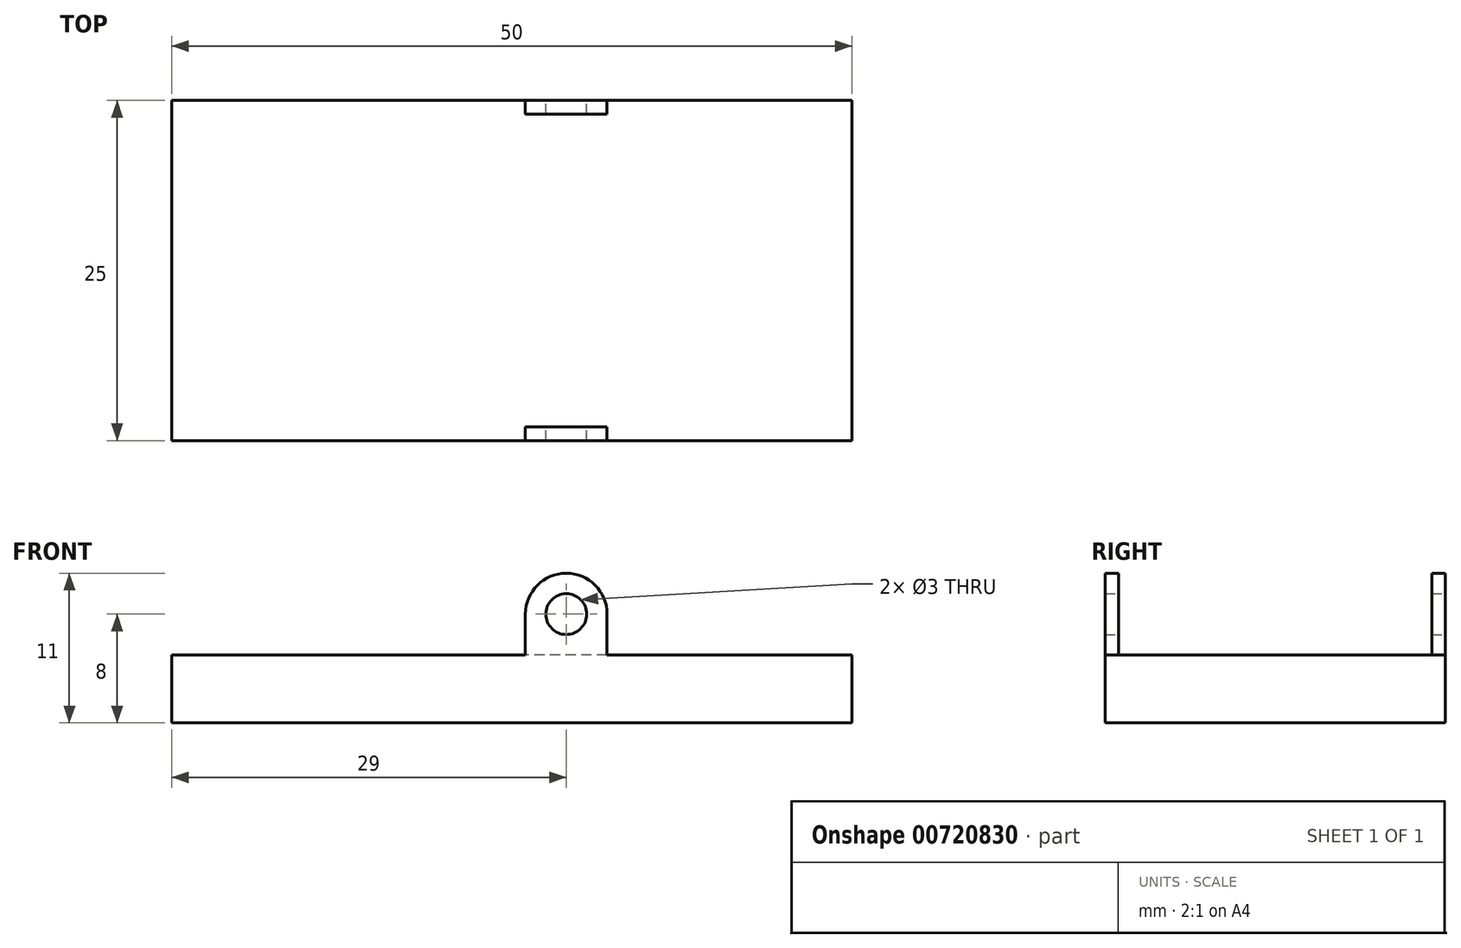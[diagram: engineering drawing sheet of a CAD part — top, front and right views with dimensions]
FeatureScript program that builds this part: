
annotation { "Feature Type Name" : "Feature", "Feature Type Description" : "" }
export const myFeature = defineFeature(function(context is Context, id is Id, definition is map)
    precondition{}
    {
        {
            var Q0;
            Q0=qCreatedBy(makeId("Top.planeOp"),FACE);
            var sketch = newSketch(context, id + "F0", { "sketchPlane" : qUnion([Q0])});
            skLineSegment(sketch, "E0.bottom", {"start": v(20, -12.5) * mm, "end": v(-20, -12.5) * mm});
            skLineSegment(sketch, "E0.top", {"start": v(20, 12.5) * mm, "end": v(-20, 12.5) * mm});
            skLineSegment(sketch, "E0.left", {"start": v(20, -12.5) * mm, "end": v(20, 12.5) * mm});
            skLineSegment(sketch, "E0.right", {"start": v(-20, -12.5) * mm, "end": v(-20, 12.5) * mm});
            skPoint(sketch, "E0.middle", {"position": v(0, 0) * mm});
            skSolve(sketch);
        }
        {
            var Q0;
            Q0=makeQuery(id+"F0.imprint","IMPRINT",FACE,{"disambiguationData":[TD([[makeQuery(id+"F0.imprint","IMPRINT",EDGE,{"derivedFrom":sQuery(id+"F0.wireOp",EDGE,"E0.bottom")}),-1.0]])]});
            extrude(context, id + "F1", {"entities" : qUnion([Q0]), "depth" : 5 * mm, "offsetDistance" : 25 * mm});
        }
        {
            var Q0;
            Q0=makeQuery(id+"F1.opExtrude","CAP_FACE",FACE,{"disambiguationData":[OSD([sQuery(id+"F0.wireOp",EDGE,"E0.bottom"),sQuery(id+"F0.wireOp",EDGE,"E0.top"),sQuery(id+"F0.wireOp",EDGE,"E0.left"),sQuery(id+"F0.wireOp",EDGE,"E0.right")])],"isStart":false});
            var sketch = newSketch(context, id + "F2", { "sketchPlane" : qUnion([Q0])});
            skLineSegment(sketch, "E1", {"start": v(20, 12.5) * mm, "end": v(12, 12.5) * mm});
            skLineSegment(sketch, "E2.bottom", {"start": v(12, 12.5) * mm, "end": v(6, 12.5) * mm});
            skLineSegment(sketch, "E2.top", {"start": v(12, -12.5) * mm, "end": v(6, -12.5) * mm});
            skLineSegment(sketch, "E2.left", {"start": v(12, 12.5) * mm, "end": v(12, -12.5) * mm});
            skLineSegment(sketch, "E2.right", {"start": v(6, 12.5) * mm, "end": v(6, -12.5) * mm});
            skSolve(sketch);
        }
        {
            var Q0;
            Q0=makeQuery(id+"FISsRW80w1BseRr_1.boolean.opBoolean","MERGE",FACE,{"derivedFrom":[makeQuery(id+"F1.opExtrude","SWEPT_FACE",FACE,{"disambiguationData":[OSD([sQuery(id+"F0.wireOp",EDGE,"E0.top")])]}),makeQuery(id+"FISsRW80w1BseRr_1.opExtrude","SWEPT_FACE",FACE,{"disambiguationData":[OSD([sQuery(id+"F2.wireOp",EDGE,"E2.bottom")])]})]});
            var sketch = newSketch(context, id + "F3", { "sketchPlane" : qUnion([Q0])});
            skLineSegment(sketch, "E3.bottom", {"start": v(-12, 11) * mm, "end": v(-6, 11) * mm});
            skLineSegment(sketch, "E3.top", {"start": v(-12, 5) * mm, "end": v(-6, 5) * mm});
            skLineSegment(sketch, "E3.left", {"start": v(-12, 11) * mm, "end": v(-12, 5) * mm});
            skLineSegment(sketch, "E3.right", {"start": v(-6, 11) * mm, "end": v(-6, 5) * mm});
            skSolve(sketch);
        }
        {
            var Q0;
            Q0=makeQuery(id+"FISsRW80w1BseRr_1.boolean.opBoolean","MERGE",FACE,{"derivedFrom":[makeQuery(id+"F1.opExtrude","SWEPT_FACE",FACE,{"disambiguationData":[OSD([sQuery(id+"F0.wireOp",EDGE,"E0.bottom")])]}),makeQuery(id+"FISsRW80w1BseRr_1.opExtrude","SWEPT_FACE",FACE,{"disambiguationData":[OSD([sQuery(id+"F2.wireOp",EDGE,"E2.top")])]})]});
            var sketch = newSketch(context, id + "F4", { "sketchPlane" : qUnion([Q0])});
            skLineSegment(sketch, "E4.bottom", {"start": v(6, 5) * mm, "end": v(12, 5) * mm});
            skLineSegment(sketch, "E4.top", {"start": v(6, 11) * mm, "end": v(12, 11) * mm});
            skLineSegment(sketch, "E4.left", {"start": v(6, 5) * mm, "end": v(6, 11) * mm});
            skLineSegment(sketch, "E4.right", {"start": v(12, 5) * mm, "end": v(12, 11) * mm});
            skSolve(sketch);
        }
        {
            var Q0;
            Q0=makeQuery(id+"F4.imprint","IMPRINT",FACE,{"disambiguationData":[TD([[makeQuery(id+"F4.imprint","IMPRINT",EDGE,{"derivedFrom":sQuery(id+"F4.wireOp",EDGE,"E4.bottom")}),-1.0]])]});
            extrude(context, id + "F5", {"entities" : qUnion([Q0]), "operationType" : NewBodyOperationType.ADD, "oppositeDirection" : true, "depth" : 1 * mm, "offsetDistance" : 25 * mm});
        }
        {
            var Q0;
            Q0=makeQuery(id+"F3.imprint","IMPRINT",FACE,{"disambiguationData":[TD([[makeQuery(id+"F3.imprint","IMPRINT",EDGE,{"derivedFrom":sQuery(id+"F3.wireOp",EDGE,"E3.bottom")}),-1.0]])]});
            extrude(context, id + "F6", {"entities" : qUnion([Q0]), "operationType" : NewBodyOperationType.ADD, "oppositeDirection" : true, "depth" : 1 * mm, "offsetDistance" : 25 * mm});
        }
        {
            var Q0;
            Q0=makeQuery(id+"F6.opExtrude","SWEPT_EDGE",EDGE,{"disambiguationData":[OSD([sQuery(id+"F3.wireOp",EDGE,"E3.bottom"),sQuery(id+"F3.wireOp",EDGE,"E3.right")])]});
            var Q1;
            Q1=makeQuery(id+"F6.opExtrude","SWEPT_EDGE",EDGE,{"disambiguationData":[OSD([sQuery(id+"F3.wireOp",EDGE,"E3.bottom"),sQuery(id+"F3.wireOp",EDGE,"E3.left")])]});
            var Q2;
            Q2=makeQuery(id+"F5.opExtrude","SWEPT_EDGE",EDGE,{"disambiguationData":[OSD([sQuery(id+"F4.wireOp",EDGE,"E4.top"),sQuery(id+"F4.wireOp",EDGE,"E4.left")])]});
            var Q3;
            Q3=makeQuery(id+"F5.opExtrude","SWEPT_EDGE",EDGE,{"disambiguationData":[OSD([sQuery(id+"F4.wireOp",EDGE,"E4.top"),sQuery(id+"F4.wireOp",EDGE,"E4.right")])]});
            fillet(context, id + "F7", {"entities" : qUnion([Q0, Q1, Q2, Q3]), "radius" : 3 * mm, "tangentPropagation" : true, "allowEdgeOverflow" : false});
        }
        {
            var Q0;
            Q0=makeQuery(id+"F6.boolean.opBoolean","MERGE",FACE,{"derivedFrom":[makeQuery(id+"F1.opExtrude","SWEPT_FACE",FACE,{"disambiguationData":[OSD([sQuery(id+"F0.wireOp",EDGE,"E0.top")])]}),makeQuery(id+"F6.opExtrude","CAP_FACE",FACE,{"disambiguationData":[OSD([sQuery(id+"F3.wireOp",EDGE,"E3.bottom"),sQuery(id+"F3.wireOp",EDGE,"E3.top"),sQuery(id+"F3.wireOp",EDGE,"E3.left"),sQuery(id+"F3.wireOp",EDGE,"E3.right")])],"isStart":true})]});
            var sketch = newSketch(context, id + "F8", { "sketchPlane" : qUnion([Q0])});
            skCircle(sketch, "E5", {"center": v(-9, 8) * mm, "radius": 1.5 * mm});
            skSolve(sketch);
        }
        {
            var Q0;
            Q0=makeQuery(id+"F8.imprint","IMPRINT",FACE,{"disambiguationData":[TD([[makeQuery(id+"F8.imprint","IMPRINT",EDGE,{"derivedFrom":sQuery(id+"F8.wireOp",EDGE,"E5")}),1.0]])]});
            extrude(context, id + "F9", {"entities" : qUnion([Q0]), "operationType" : NewBodyOperationType.REMOVE, "oppositeDirection" : true, "depth" : 30 * mm, "offsetDistance" : 25 * mm});
        }
        {
            var Q0;
            Q0=makeQuery(id+"F1.opExtrude","SWEPT_FACE",FACE,{"disambiguationData":[OSD([sQuery(id+"F0.wireOp",EDGE,"E0.left")])]});
            extrude(context, id + "F10", {"entities" : qUnion([Q0]), "operationType" : NewBodyOperationType.ADD, "depth" : 10 * mm, "offsetDistance" : 25 * mm});
        }
    });
